# Revit family: 35816-presto
name_source: partatom
category: Plumbing Fixtures
units: mm (PartAtom-declared; Revit-internal decimal feet)

## family parameters
Always vertical = Yes
Cut with Voids When Loaded = No
Maintain Annotation Orientation = No
OmniClass Number = 23.45.00.00
OmniClass Title = Sanitary, Laundry, and Cleaning Equipment
Part Type = Normal
Room Calculation Point = No
Round Connector Dimension = Use Diameter
Shared = No
Work Plane-Based = Yes

## types (1)
- 35816 -presto
    Default Elevation = 1219 mm
    Description = Timed flow mixer tap for shower
    Manufacturer = presto
    Model = 35816
    RANGE = Timed flow mixer tap for shower
    Thermal resistance = 75 (h·ft²·°F)/BTU
    URL = https://www.prestodatashare.com
    brand = LES ROBINETS PRESTO
    min flow = 4 L/min
    min pressure = 3.00 bar
    ref = 35816 - "Ready-To-Install" NF IB PRESTO ALPA mixer tap

## geometry (parser evidence)
native form markers: Sweep x2
no freeform markers — native parametric forms only
